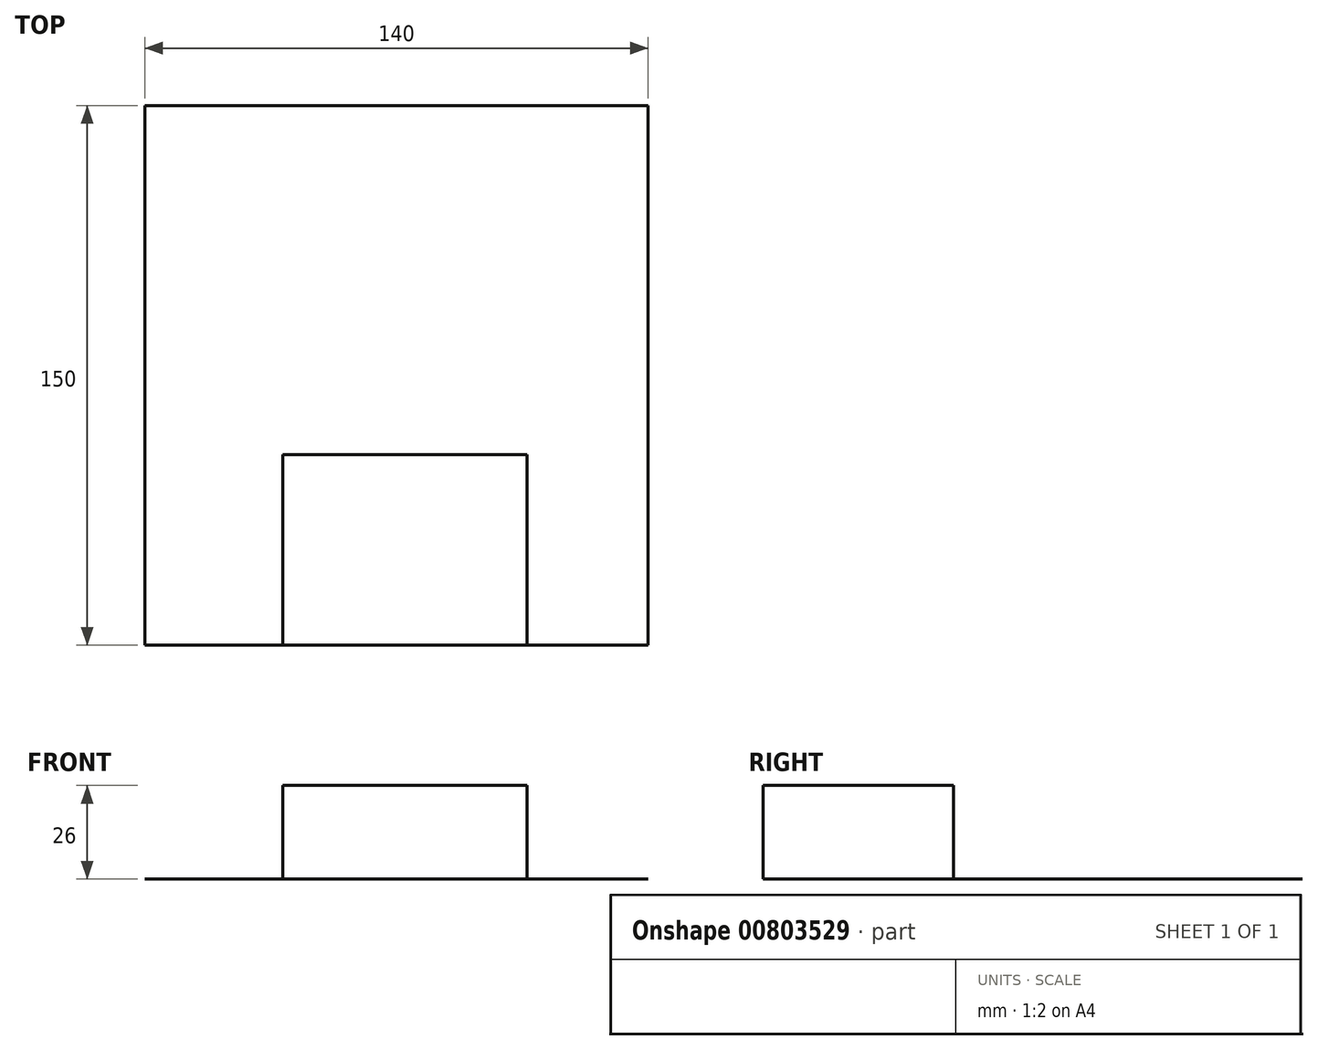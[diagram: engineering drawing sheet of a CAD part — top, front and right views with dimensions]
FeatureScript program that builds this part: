
annotation { "Feature Type Name" : "Feature", "Feature Type Description" : "" }
export const myFeature = defineFeature(function(context is Context, id is Id, definition is map)
    precondition{}
    {
        {
            var Q0;
            Q0=qCreatedBy(makeId("Top.planeOp"),FACE);
            var sketch = newSketch(context, id + "F0", { "sketchPlane" : qUnion([Q0])});
            skLineSegment(sketch, "E0.bottom", {"start": v(0, 0) * mm, "end": v(140, 0) * mm});
            skLineSegment(sketch, "E0.top", {"start": v(0, 150) * mm, "end": v(140, 150) * mm});
            skLineSegment(sketch, "E0.left", {"start": v(0, 0) * mm, "end": v(0, 150) * mm});
            skLineSegment(sketch, "E0.right", {"start": v(140, 0) * mm, "end": v(140, 150) * mm});
            skLineSegment(sketch, "E1.bottom", {"start": v(38.4, 0) * mm, "end": v(106.4, 0) * mm});
            skLineSegment(sketch, "E1.top", {"start": v(38.4, 53) * mm, "end": v(106.4, 53) * mm});
            skLineSegment(sketch, "E1.left", {"start": v(38.4, 0) * mm, "end": v(38.4, 53) * mm});
            skLineSegment(sketch, "E1.right", {"start": v(106.4, 0) * mm, "end": v(106.4, 53) * mm});
            skSolve(sketch);
        }
        {
            var Q0;
            Q0=makeQuery(id+"F0.imprint","IMPRINT",FACE,{"disambiguationData":[TD([[makeQuery(id+"F0.imprint","IMPRINT",EDGE,{"derivedFrom":sQuery(id+"F0.wireOp",EDGE,"E0.top")}),-1.0]])]});
            var Q1;
            Q1=makeQuery(id+"F0.imprint","IMPRINT",FACE,{"disambiguationData":[TD([[makeQuery(id+"F0.imprint","IMPRINT",EDGE,{"derivedFrom":sQuery(id+"F0.wireOp",EDGE,"E1.top")}),-1.0]])]});
            extrude(context, id + "F1", {"entities" : qUnion([Q0, Q1]), "depth" : 1 / 406.4 * mm, "offsetDistance" : 25.4 * mm});
        }
        {
            var Q0;
            Q0=makeQuery(id+"F0.imprint","IMPRINT",FACE,{"disambiguationData":[TD([[makeQuery(id+"F0.imprint","IMPRINT",EDGE,{"derivedFrom":sQuery(id+"F0.wireOp",EDGE,"E1.top")}),-1.0]])]});
            extrude(context, id + "F2", {"entities" : qUnion([Q0]), "operationType" : NewBodyOperationType.ADD, "depth" : 26 * mm, "offsetDistance" : 25.4 * mm});
        }
    });
